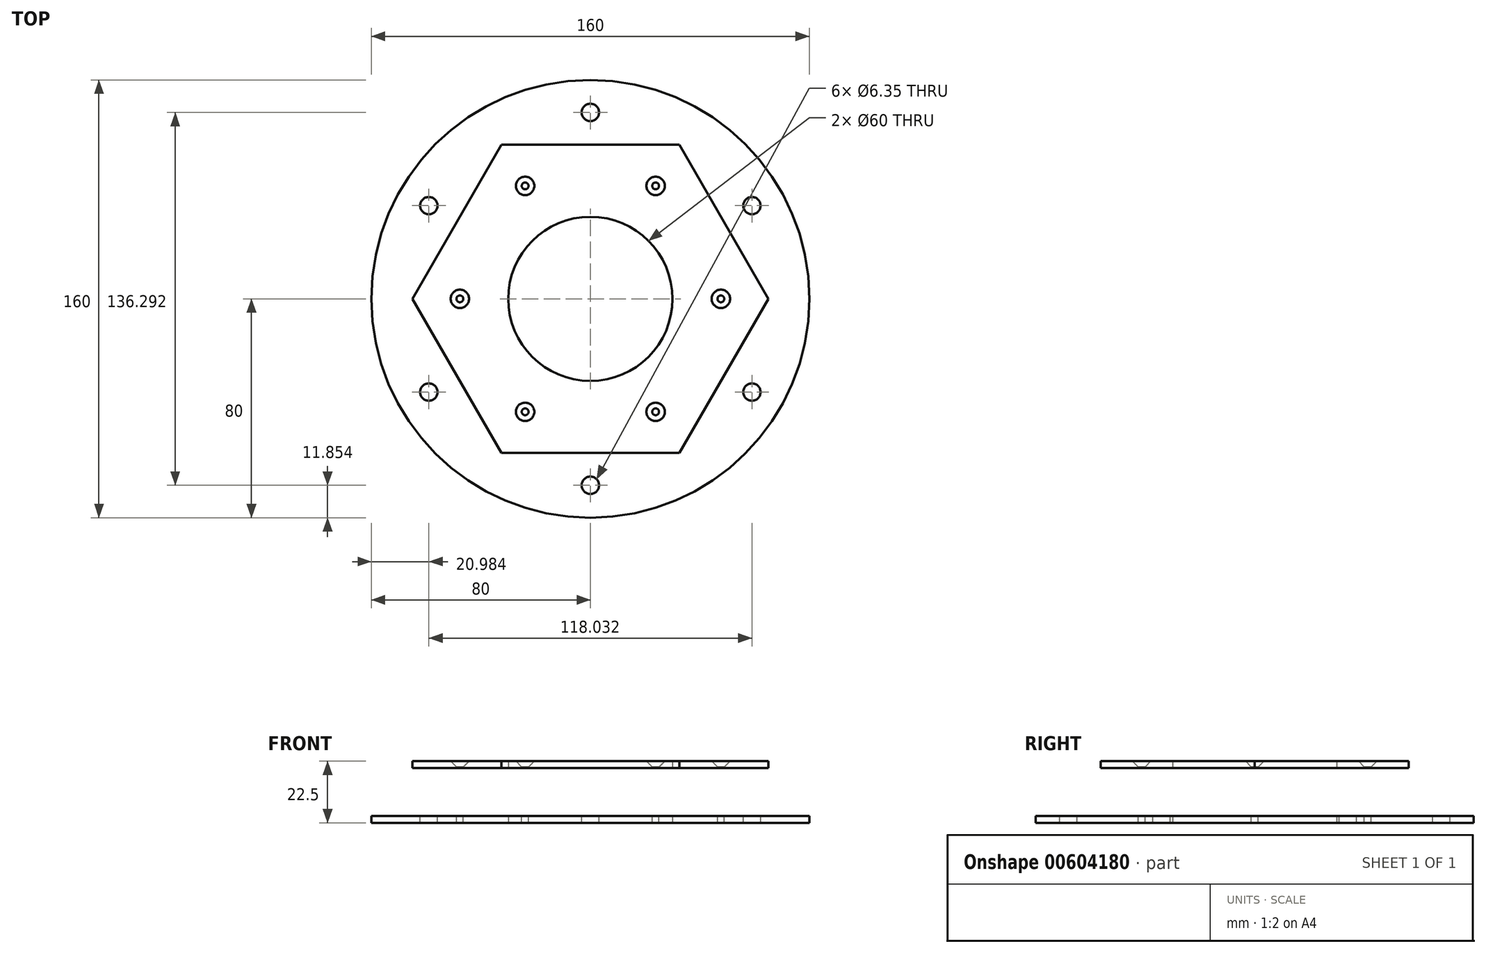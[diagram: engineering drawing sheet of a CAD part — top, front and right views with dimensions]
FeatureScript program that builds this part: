
annotation { "Feature Type Name" : "Feature", "Feature Type Description" : "" }
export const myFeature = defineFeature(function(context is Context, id is Id, definition is map)
    precondition{}
    {
        {
            var Q0;
            Q0=qCreatedBy(makeId("Top.planeOp"),FACE);
            var sketch = newSketch(context, id + "F0", { "sketchPlane" : qUnion([Q0])});
            skCircle(sketch, "E0.cCircle", {"center": v(0, 0) * mm, "radius": 56.3 * mm, "construction": true});
            skLineSegment(sketch, "E0.0", {"start": v(32.5, 56.3) * mm, "end": v(65, 0) * mm});
            skLineSegment(sketch, "E0.1", {"start": v(65, 0) * mm, "end": v(32.5, -56.3) * mm});
            skLineSegment(sketch, "E0.2", {"start": v(32.5, -56.3) * mm, "end": v(-32.5, -56.3) * mm});
            skLineSegment(sketch, "E0.3", {"start": v(-32.5, -56.3) * mm, "end": v(-65, 0) * mm});
            skLineSegment(sketch, "E0.4", {"start": v(-65, 0) * mm, "end": v(-32.5, 56.3) * mm});
            skLineSegment(sketch, "E0.5", {"start": v(-32.5, 56.3) * mm, "end": v(32.5, 56.3) * mm});
            skPoint(sketch, "E0.0.midPoint", {"position": v(48.75, 28.15) * mm});
            skPoint(sketch, "E1.0.midPoint", {"position": v(31.43, 18.15) * mm});
            skLineSegment(sketch, "E2", {"start": v(-32.5, 56.3) * mm, "end": v(-20.95, 36.3) * mm, "construction": true});
            skLineSegment(sketch, "E3", {"start": v(32.5, 56.3) * mm, "end": v(20.95, 36.3) * mm, "construction": true});
            skLineSegment(sketch, "E4", {"start": v(65, 0) * mm, "end": v(41.9, 0) * mm, "construction": true});
            skLineSegment(sketch, "E5", {"start": v(20.95, -36.3) * mm, "end": v(32.5, -56.3) * mm, "construction": true});
            skLineSegment(sketch, "E6", {"start": v(-20.95, -36.3) * mm, "end": v(-32.5, -56.3) * mm, "construction": true});
            skLineSegment(sketch, "E7", {"start": v(-41.9, 0) * mm, "end": v(-65, 0) * mm, "construction": true});
            skCircle(sketch, "E8", {"center": v(0, 0) * mm, "radius": 80 * mm});
            skCircle(sketch, "E9", {"center": v(0, 0) * mm, "radius": 30 * mm});
            skSolve(sketch);
        }
        {
            var Q0;
            Q0 = qSketchRegion(id + "F0", true);
            var Q1;
            Q1=makeQuery(id+"F0.imprint","IMPRINT",FACE,{"disambiguationData":[TD([[makeQuery(id+"F0.imprint","IMPRINT",EDGE,{"derivedFrom":sQuery(id+"F0.wireOp",EDGE,"E0.0")}),-1.0]])]});
            extrude(context, id + "F1", {"entities" : qUnion([Q0, Q1]), "depth" : 2.5 * mm, "offsetDistance" : 25 * mm});
        }
        {
            var Q0;
            Q0=qCreatedBy(makeId("Top.planeOp"),FACE);
            cPlane(context, id + "F2", {"entities" : qUnion([Q0]), "cplaneType" : CPlaneType.OFFSET, "offset" : 20 * mm, "width" : 150 * mm, "height" : 150 * mm});
        }
        {
            var Q0;
            Q0=qCreatedBy(id+"F2.planeOp",FACE);
            var sketch = newSketch(context, id + "F3", { "sketchPlane" : qUnion([Q0])});
            skCircle(sketch, "E10.cCircle", {"center": v(0, 0) * mm, "radius": 56.3 * mm, "construction": true});
            skLineSegment(sketch, "E10.0", {"start": v(32.5, 56.3) * mm, "end": v(65, 0) * mm});
            skLineSegment(sketch, "E10.1", {"start": v(65, 0) * mm, "end": v(32.5, -56.3) * mm});
            skLineSegment(sketch, "E10.2", {"start": v(32.5, -56.3) * mm, "end": v(-32.5, -56.3) * mm});
            skLineSegment(sketch, "E10.3", {"start": v(-32.5, -56.3) * mm, "end": v(-65, 0) * mm});
            skLineSegment(sketch, "E10.4", {"start": v(-65, 0) * mm, "end": v(-32.5, 56.3) * mm});
            skLineSegment(sketch, "E10.5", {"start": v(-32.5, 56.3) * mm, "end": v(32.5, 56.3) * mm});
            skPoint(sketch, "E10.0.midPoint", {"position": v(48.75, 28.15) * mm});
            skPoint(sketch, "E11.0.midPoint", {"position": v(31.43, -18.15) * mm});
            skCircle(sketch, "E12", {"center": v(0, 0) * mm, "radius": 30 * mm});
            skSolve(sketch);
        }
        {
            var Q0;
            Q0 = qSketchRegion(id + "F3", true);
            extrude(context, id + "F4", {"entities" : qUnion([Q0]), "depth" : 2.5 * mm, "offsetDistance" : 25 * mm});
        }
        {
            var Q0;
            Q0=makeQuery(id+"F4.opExtrude","CAP_FACE",FACE,{"disambiguationData":[OSD([sQuery(id+"F3.wireOp",EDGE,"E10.0"),sQuery(id+"F3.wireOp",EDGE,"E10.1"),sQuery(id+"F3.wireOp",EDGE,"E10.2"),sQuery(id+"F3.wireOp",EDGE,"E10.3"),sQuery(id+"F3.wireOp",EDGE,"E10.4"),sQuery(id+"F3.wireOp",EDGE,"E10.5"),sQuery(id+"F3.wireOp",EDGE,"E11.0"),sQuery(id+"F3.wireOp",EDGE,"E11.1"),sQuery(id+"F3.wireOp",EDGE,"E11.2"),sQuery(id+"F3.wireOp",EDGE,"E11.3"),sQuery(id+"F3.wireOp",EDGE,"E11.4"),sQuery(id+"F3.wireOp",EDGE,"E11.5")])],"isStart":false});
            var sketch = newSketch(context, id + "F5", { "sketchPlane" : qUnion([Q0])});
            skLineSegment(sketch, "E13", {"start": v(-32.5, 56.3) * mm, "end": v(-15.18, 26.3) * mm, "construction": true});
            skLineSegment(sketch, "E14", {"start": v(32.5, 56.3) * mm, "end": v(15.18, 26.3) * mm, "construction": true});
            skLineSegment(sketch, "E15", {"start": v(65, 0) * mm, "end": v(30.36, 0) * mm, "construction": true});
            skLineSegment(sketch, "E16", {"start": v(32.5, -56.3) * mm, "end": v(15.18, -26.3) * mm, "construction": true});
            skLineSegment(sketch, "E17", {"start": v(-32.5, -56.3) * mm, "end": v(-15.18, -26.3) * mm, "construction": true});
            skLineSegment(sketch, "E18", {"start": v(-65, 0) * mm, "end": v(-30.36, 0) * mm, "construction": true});
            skPoint(sketch, "E19", {"position": v(-23.84, 41.3) * mm});
            skPoint(sketch, "E20", {"position": v(23.84, 41.3) * mm});
            skPoint(sketch, "E21", {"position": v(47.68, 0) * mm});
            skPoint(sketch, "E22", {"position": v(23.84, -41.3) * mm});
            skPoint(sketch, "E23", {"position": v(-23.84, -41.3) * mm});
            skPoint(sketch, "E24", {"position": v(-47.68, 0) * mm});
            skSolve(sketch);
        }
        {
            var Q0;
            Q0=sQuery(id+"F5.wireOp",VERTEX,"E19");
            var Q1;
            Q1=sQuery(id+"F5.wireOp",VERTEX,"E20");
            var Q2;
            Q2=sQuery(id+"F5.wireOp",VERTEX,"E21");
            var Q3;
            Q3=sQuery(id+"F5.wireOp",VERTEX,"E22");
            var Q4;
            Q4=sQuery(id+"F5.wireOp",VERTEX,"E23");
            var Q5;
            Q5=sQuery(id+"F5.wireOp",VERTEX,"E24");
            var Q6;
            Q6=makeQuery(id+"F4.opExtrude","SWEPT_BODY",BODY,{"disambiguationData":[OSD([sQuery(id+"F3.wireOp",EDGE,"E10.0"),sQuery(id+"F3.wireOp",EDGE,"E10.1"),sQuery(id+"F3.wireOp",EDGE,"E10.2"),sQuery(id+"F3.wireOp",EDGE,"E10.3"),sQuery(id+"F3.wireOp",EDGE,"E10.4"),sQuery(id+"F3.wireOp",EDGE,"E10.5"),sQuery(id+"F3.wireOp",EDGE,"E12")])]});
            var Q7;
            Q7=makeQuery(id+"F1.opExtrude","SWEPT_BODY",BODY,{"disambiguationData":[OSD([sQuery(id+"F0.wireOp",EDGE,"E8"),sQuery(id+"F0.wireOp",EDGE,"E9")])]});
            hole(context, id + "F6", {"style" : HoleStyle.C_SINK, "endStyle" : HoleEndStyle.THROUGH, "standardTappedOrClearance" : lookupTablePath({ "standard" : "ISO", "engagement" : "75%", "pitch" : "0.5 mm", "size" : "M3", "type" : "Tapped" }), "standardBlindInLast" : lookupTablePath({ "standard" : "ISO", "engagement" : "75%", "pitch" : "0.5 mm", "size" : "M3", "type" : "Tapped" }), "holeDiameter" : 2.5 * mm, "cSinkDiameter" : 6.72 * mm, "cSinkAngle" : 90 * degree, "majorDiameter" : 3 * mm, "showTappedDepth" : true, "isTappedThrough" : true, "tappedDepth" : 12 * mm, "tapClearance" : 3, "locations" : qUnion([Q0, Q1, Q2, Q3, Q4, Q5]), "scope" : qUnion([Q6, Q7])});
        }
        {
            var Q0;
            Q0=makeQuery(id+"F1.opExtrude","CAP_FACE",FACE,{"disambiguationData":[OSD([sQuery(id+"F0.wireOp",EDGE,"E1.0"),sQuery(id+"F0.wireOp",EDGE,"E1.1"),sQuery(id+"F0.wireOp",EDGE,"E1.2"),sQuery(id+"F0.wireOp",EDGE,"E1.3"),sQuery(id+"F0.wireOp",EDGE,"E1.4"),sQuery(id+"F0.wireOp",EDGE,"E1.5"),sQuery(id+"F0.wireOp",EDGE,"E8")])],"isStart":false});
            var sketch = newSketch(context, id + "F7", { "sketchPlane" : qUnion([Q0])});
            skCircle(sketch, "E25", {"center": v(0, 0) * mm, "radius": 80 * mm, "construction": true});
            skCircle(sketch, "E26.cCircle", {"center": v(0, 0) * mm, "radius": 56.3 * mm, "construction": true});
            skLineSegment(sketch, "E26.0", {"start": v(32.5, 56.3) * mm, "end": v(65, 0) * mm, "construction": true});
            skLineSegment(sketch, "E26.1", {"start": v(65, 0) * mm, "end": v(32.5, -56.3) * mm, "construction": true});
            skLineSegment(sketch, "E26.2", {"start": v(32.5, -56.3) * mm, "end": v(-32.5, -56.3) * mm, "construction": true});
            skLineSegment(sketch, "E26.3", {"start": v(-32.5, -56.3) * mm, "end": v(-65, 0) * mm, "construction": true});
            skLineSegment(sketch, "E26.4", {"start": v(-65, 0) * mm, "end": v(-32.5, 56.3) * mm, "construction": true});
            skLineSegment(sketch, "E26.5", {"start": v(-32.5, 56.3) * mm, "end": v(32.5, 56.3) * mm, "construction": true});
            skPoint(sketch, "E26.0.midPoint", {"position": v(48.75, 28.15) * mm});
            skLineSegment(sketch, "E27", {"start": v(0, 56.3) * mm, "end": v(0, 80) * mm, "construction": true});
            skLineSegment(sketch, "E28", {"start": v(48.75, 28.15) * mm, "end": v(69.28, 40) * mm, "construction": true});
            skLineSegment(sketch, "E29", {"start": v(48.75, -28.15) * mm, "end": v(69.28, -40) * mm, "construction": true});
            skLineSegment(sketch, "E30", {"start": v(0, -56.3) * mm, "end": v(0, -80) * mm, "construction": true});
            skLineSegment(sketch, "E31", {"start": v(-48.75, -28.15) * mm, "end": v(-69.28, -40) * mm, "construction": true});
            skLineSegment(sketch, "E32", {"start": v(-48.75, 28.15) * mm, "end": v(-69.28, 40) * mm, "construction": true});
            skPoint(sketch, "E33", {"position": v(0, 68.15) * mm});
            skPoint(sketch, "E34", {"position": v(59.02, 34.07) * mm});
            skPoint(sketch, "E35", {"position": v(59.02, -34.07) * mm});
            skPoint(sketch, "E36", {"position": v(0, -68.15) * mm});
            skPoint(sketch, "E37", {"position": v(-59.02, 34.07) * mm});
            skPoint(sketch, "E38", {"position": v(-59.02, -34.07) * mm});
            skSolve(sketch);
        }
        {
            var Q0;
            Q0=sQuery(id+"F7.wireOp",VERTEX,"E33");
            var Q1;
            Q1=sQuery(id+"F7.wireOp",VERTEX,"E34");
            var Q2;
            Q2=sQuery(id+"F7.wireOp",VERTEX,"E35");
            var Q3;
            Q3=sQuery(id+"F7.wireOp",VERTEX,"E36");
            var Q4;
            Q4=sQuery(id+"F7.wireOp",VERTEX,"E38");
            var Q5;
            Q5=sQuery(id+"F7.wireOp",VERTEX,"E37");
            var Q6;
            Q6=makeQuery(id+"F1.opExtrude","SWEPT_BODY",BODY,{"disambiguationData":[OSD([sQuery(id+"F0.wireOp",EDGE,"E1.0"),sQuery(id+"F0.wireOp",EDGE,"E1.1"),sQuery(id+"F0.wireOp",EDGE,"E1.2"),sQuery(id+"F0.wireOp",EDGE,"E1.3"),sQuery(id+"F0.wireOp",EDGE,"E1.4"),sQuery(id+"F0.wireOp",EDGE,"E1.5"),sQuery(id+"F0.wireOp",EDGE,"E8")])]});
            hole(context, id + "F8", {"style" : HoleStyle.SIMPLE, "endStyle" : HoleEndStyle.THROUGH, "holeDiameter" : 6.35 * mm, "majorDiameter" : 5 * mm, "isTappedThrough" : true, "tappedDepth" : 12 * mm, "tapClearance" : 3, "locations" : qUnion([Q0, Q1, Q2, Q3, Q4, Q5]), "scope" : qUnion([Q6])});
        }
    });
